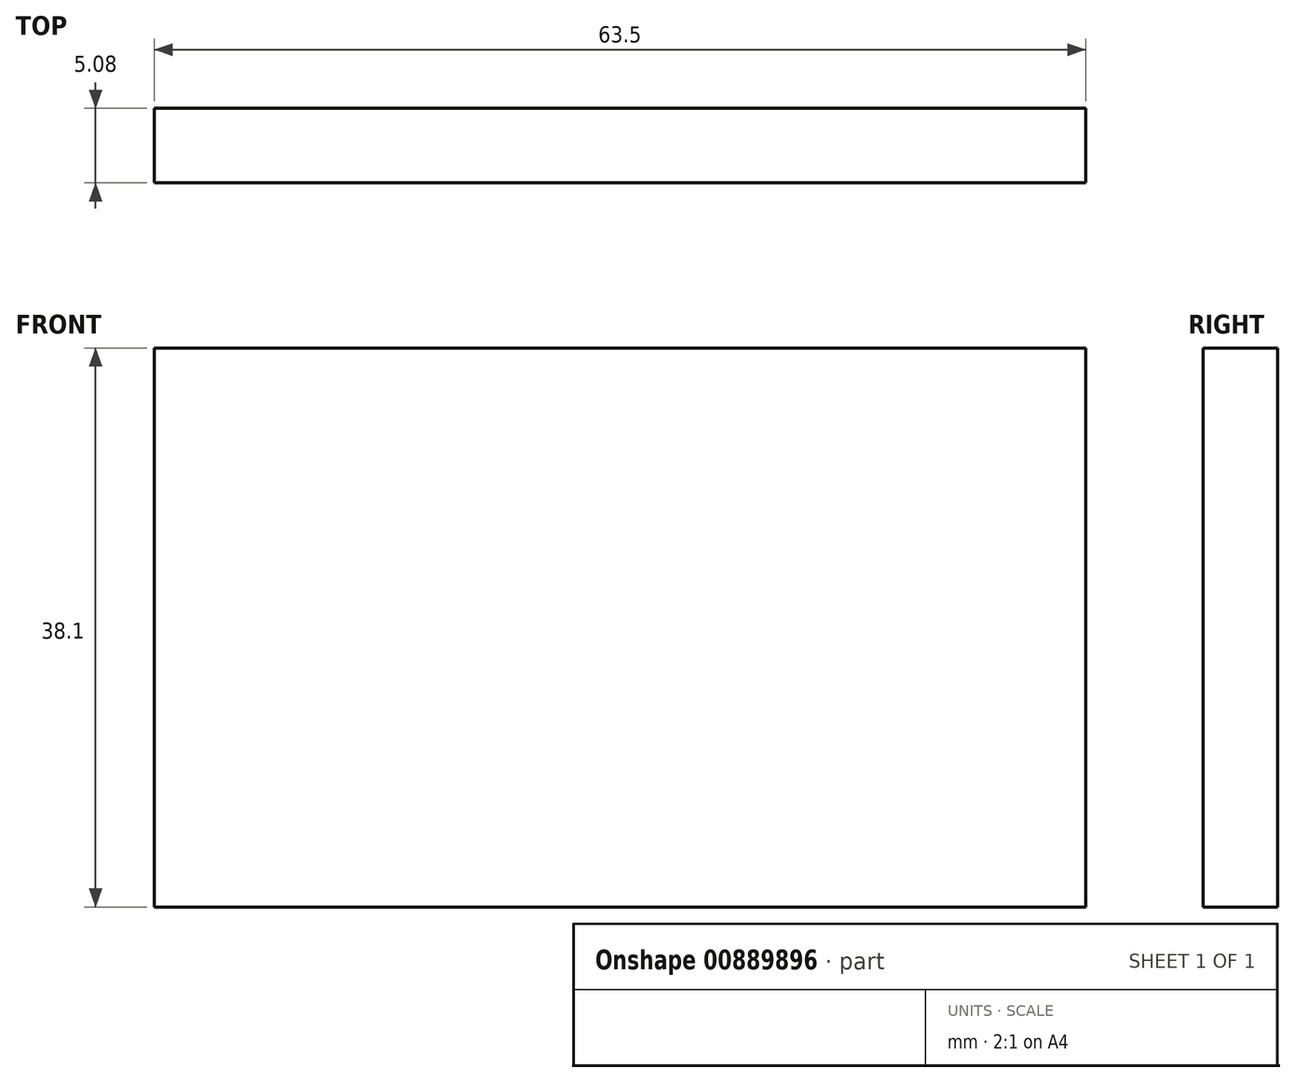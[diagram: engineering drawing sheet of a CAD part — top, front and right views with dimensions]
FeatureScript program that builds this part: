
annotation { "Feature Type Name" : "Feature", "Feature Type Description" : "" }
export const myFeature = defineFeature(function(context is Context, id is Id, definition is map)
    precondition{}
    {
        {
            var Q0;
            Q0=qCreatedBy(makeId("Front.planeOp"),FACE);
            var sketch = newSketch(context, id + "F0", { "sketchPlane" : qUnion([Q0])});
            skLineSegment(sketch, "E0.bottom", {"start": v(0, 0) * mm, "end": v(63.5, 0) * mm});
            skLineSegment(sketch, "E0.top", {"start": v(0, 38.1) * mm, "end": v(63.5, 38.1) * mm});
            skLineSegment(sketch, "E0.left", {"start": v(0, 0) * mm, "end": v(0, 38.1) * mm});
            skLineSegment(sketch, "E0.right", {"start": v(63.5, 0) * mm, "end": v(63.5, 38.1) * mm});
            skSolve(sketch);
        }
        {
            var Q0;
            Q0 = qSketchRegion(id + "F0", true);
            extrude(context, id + "F1", {"entities" : qUnion([Q0]), "depth" : 5.08 * mm, "offsetDistance" : 25.4 * mm});
        }
    });
